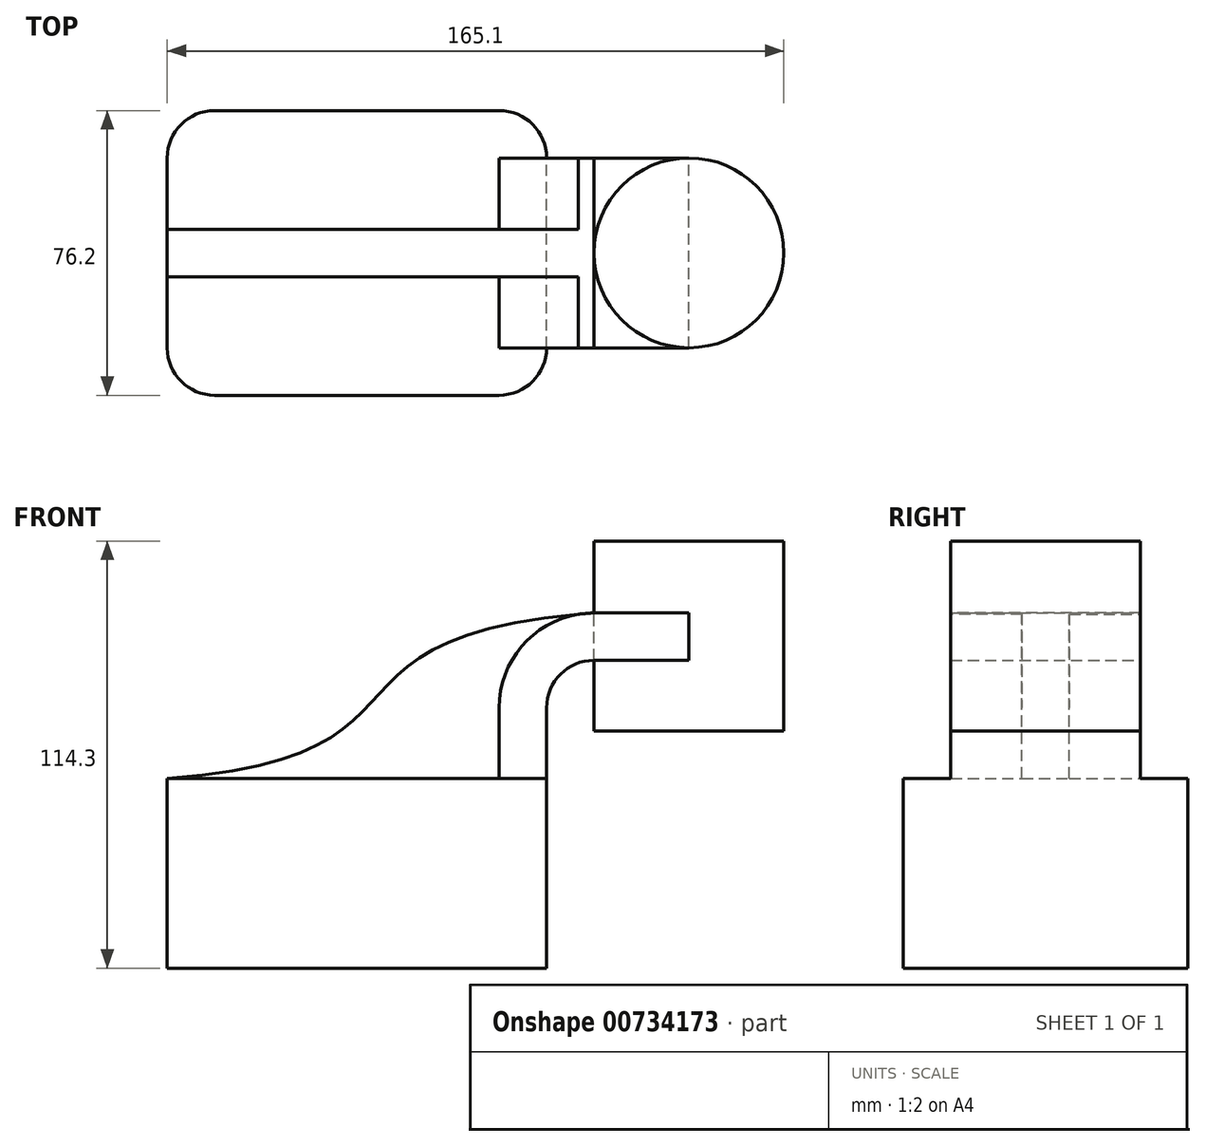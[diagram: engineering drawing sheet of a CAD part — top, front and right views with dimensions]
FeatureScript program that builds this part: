
annotation { "Feature Type Name" : "Feature", "Feature Type Description" : "" }
export const myFeature = defineFeature(function(context is Context, id is Id, definition is map)
    precondition{}
    {
        {
            var Q0;
            Q0=qCreatedBy(makeId("Front.planeOp"),FACE);
            var sketch = newSketch(context, id + "F0", { "sketchPlane" : qUnion([Q0])});
            skLineSegment(sketch, "E0.bottom", {"start": v(50.8, 25.4) * mm, "end": v(-50.8, 25.4) * mm});
            skLineSegment(sketch, "E0.top", {"start": v(50.8, -25.4) * mm, "end": v(-50.8, -25.4) * mm});
            skLineSegment(sketch, "E0.left", {"start": v(50.8, 25.4) * mm, "end": v(50.8, -25.4) * mm});
            skLineSegment(sketch, "E0.right", {"start": v(-50.8, 25.4) * mm, "end": v(-50.8, -25.4) * mm});
            skPoint(sketch, "E0.middle", {"position": v(0, 0) * mm});
            skLineSegment(sketch, "E1.bottom", {"start": v(114.3, 88.9) * mm, "end": v(88.9, 88.9) * mm});
            skLineSegment(sketch, "E1.top", {"start": v(114.3, 38.1) * mm, "end": v(88.9, 38.1) * mm});
            skLineSegment(sketch, "E1.left", {"start": v(114.3, 88.9) * mm, "end": v(114.3, 38.1) * mm});
            skLineSegment(sketch, "E1.right", {"start": v(88.9, 88.9) * mm, "end": v(88.9, 38.1) * mm});
            skPoint(sketch, "E1.middle", {"position": v(101.6, 63.5) * mm});
            skLineSegment(sketch, "E2", {"start": v(50.8, 25.4) * mm, "end": v(50.8, 44.27) * mm});
            skArc(sketch, "E3", {"start": v(50.8, 44.27) * mm, "mid": v(54.52, 53.25) * mm, "end": v(63.5, 56.97) * mm});
            skLineSegment(sketch, "E4", {"start": v(63.5, 56.97) * mm, "end": v(88.9, 56.97) * mm});
            skLineSegment(sketch, "E5.0", {"start": v(63.5, 69.67) * mm, "end": v(88.9, 69.67) * mm});
            skArc(sketch, "E5.1", {"start": v(38.1, 44.27) * mm, "mid": v(45.54, 62.23) * mm, "end": v(63.5, 69.67) * mm});
            skLineSegment(sketch, "E5.2", {"start": v(38.1, 25.4) * mm, "end": v(38.1, 44.27) * mm});
            skLineSegment(sketch, "E6", {"start": v(88.9, 69.67) * mm, "end": v(88.9, 56.97) * mm});
            skFitSpline(sketch, "E7", {"points": [v(-50.8, 25.4) * mm, v(63.5, 69.67) * mm], "startDerivative": vector(233.71, 17.4) * mm, "endDerivative": vector(241.25, 18.46) * mm});
            skSolve(sketch);
        }
        {
            var Q0;
            Q0=makeQuery(id+"F0.imprint","IMPRINT",FACE,{"disambiguationData":[TD([[makeQuery(id+"F0.imprint","IMPRINT",EDGE,{"derivedFrom":sQuery(id+"F0.wireOp",EDGE,"E0.top")}),-1.0]])]});
            extrude(context, id + "F1", {"entities" : qUnion([Q0]), "endBound" : BoundingType.SYMMETRIC, "depth" : 76.2 * mm, "offsetDistance" : 25.4 * mm});
        }
        {
            var Q0;
            {var subQ1=sQuery(id+"F0.wireOp",EDGE,"E2");Q0=makeQuery(id+"F0.imprint","IMPRINT",FACE,{"disambiguationData":[TD([[makeQuery(id+"F0.imprint","IMPRINT",EDGE,{"derivedFrom":subQ1}),1.0]])]});}
            var Q1;
            {var subQ5=sQuery(id+"F0.wireOp",EDGE,"E6");Q1=makeQuery(id+"F0.imprint","IMPRINT",FACE,{"disambiguationData":[TD([[makeQuery(id+"F0.imprint","IMPRINT",EDGE,{"derivedFrom":subQ5}),-1.0]])]});}
            extrude(context, id + "F2", {"entities" : qUnion([Q0, Q1]), "operationType" : NewBodyOperationType.ADD, "endBound" : BoundingType.SYMMETRIC, "depth" : 50.8 * mm, "offsetDistance" : 25.4 * mm});
        }
        {
            var Q0;
            {var subQ3=sQuery(id+"F0.wireOp",EDGE,"E5.2");Q0=makeQuery(id+"F0.imprint","IMPRINT",FACE,{"disambiguationData":[TD([[makeQuery(id+"F0.imprint","IMPRINT",EDGE,{"derivedFrom":subQ3}),1.0]])]});}
            extrude(context, id + "F3", {"entities" : qUnion([Q0]), "operationType" : NewBodyOperationType.ADD, "endBound" : BoundingType.SYMMETRIC, "depth" : 12.7 * mm, "offsetDistance" : 25.4 * mm});
        }
        {
            var Q0;
            {var subQ1=sQuery(id+"F0.wireOp",EDGE,"E1.bottom");Q0=makeQuery(id+"F0.imprint","IMPRINT",FACE,{"disambiguationData":[TD([[makeQuery(id+"F0.imprint","IMPRINT",EDGE,{"derivedFrom":subQ1}),1.0]])]});}
            var Q1;
            Q1=sQuery(id+"F0.wireOp",EDGE,"E1.right");
            revolve(context, id + "F4", {"surfaceOperationType" : NewSurfaceOperationType.NEW, "entities" : qUnion([Q0]), "axis" : qUnion([Q1]), "revolveType" : RevolveType.FULL});
        }
        {
            var Q0;
            Q0=makeQuery(id+"F1.opExtrude","CAP_EDGE",EDGE,{"disambiguationData":[OSD([sQuery(id+"F0.wireOp",EDGE,"E0.right")])],"isStart":false});
            var Q1;
            Q1=makeQuery(id+"F1.opExtrude","CAP_EDGE",EDGE,{"disambiguationData":[OSD([sQuery(id+"F0.wireOp",EDGE,"E0.left")])],"isStart":false});
            var Q2;
            Q2=makeQuery(id+"F1.opExtrude","CAP_EDGE",EDGE,{"disambiguationData":[OSD([sQuery(id+"F0.wireOp",EDGE,"E0.left")])],"isStart":true});
            var Q3;
            Q3=makeQuery(id+"F1.opExtrude","CAP_EDGE",EDGE,{"disambiguationData":[OSD([sQuery(id+"F0.wireOp",EDGE,"E0.right")])],"isStart":true});
            fillet(context, id + "F5", {"entities" : qUnion([Q0, Q1, Q2, Q3]), "radius" : 12.7 * mm, "tangentPropagation" : true, "allowEdgeOverflow" : false});
        }
    });
